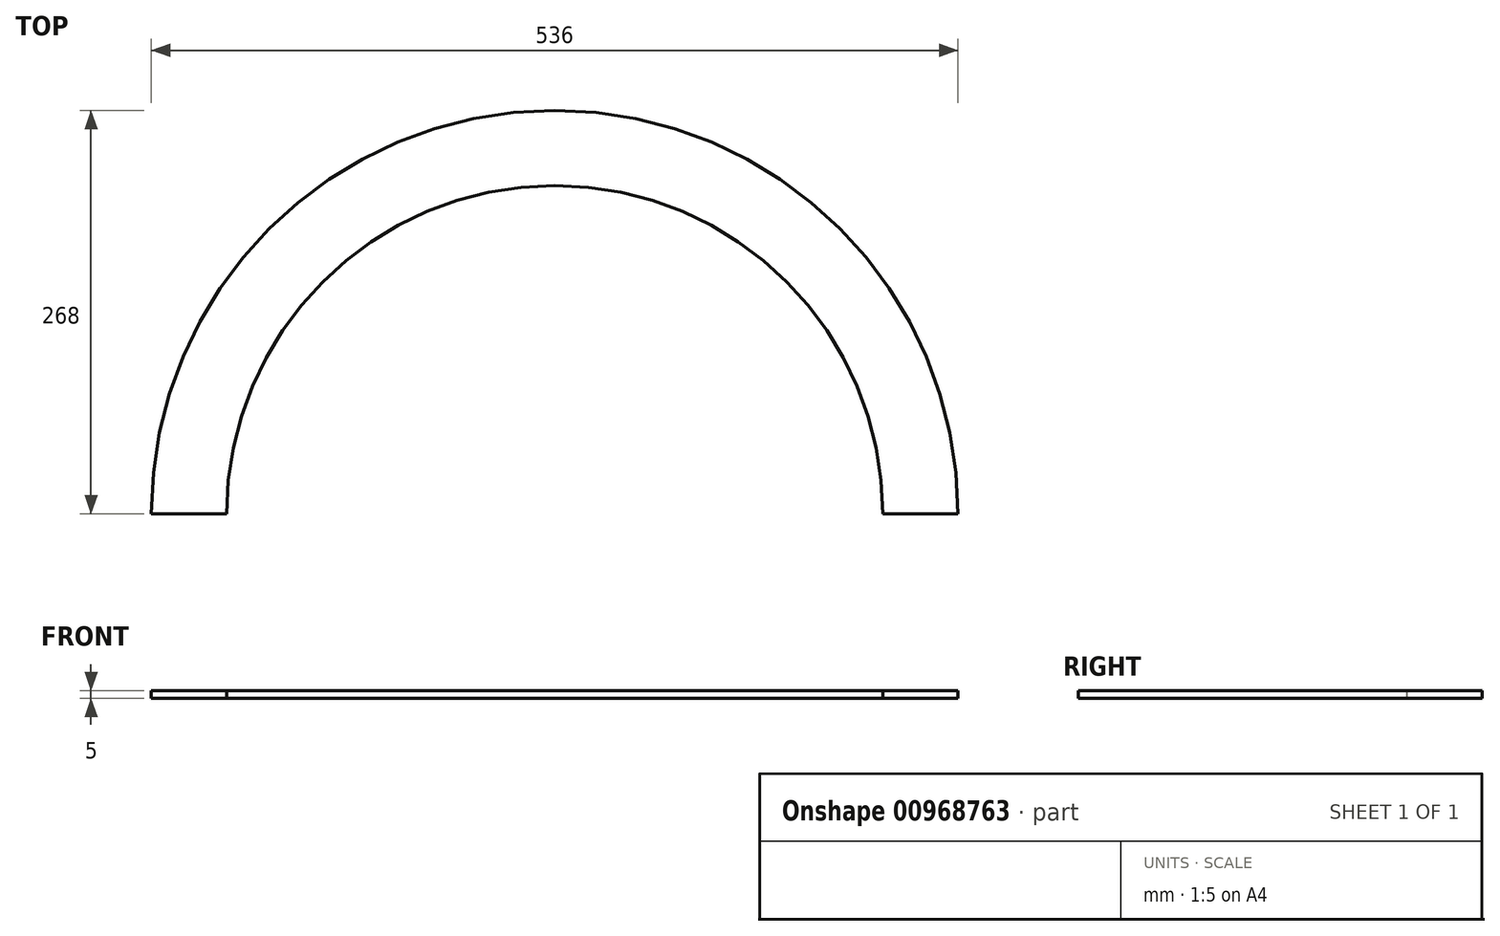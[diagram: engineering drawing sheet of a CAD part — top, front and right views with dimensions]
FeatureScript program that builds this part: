
annotation { "Feature Type Name" : "Feature", "Feature Type Description" : "" }
export const myFeature = defineFeature(function(context is Context, id is Id, definition is map)
    precondition{}
    {
        {
            var Q0;
            Q0=qCreatedBy(makeId("Top.planeOp"),FACE);
            var sketch = newSketch(context, id + "F0", { "sketchPlane" : qUnion([Q0])});
            skArc(sketch, "E0", {"start": v(218, 0) * mm, "mid": v(0, 218) * mm, "end": v(-218, 0) * mm});
            skArc(sketch, "E1", {"start": v(268, 0) * mm, "mid": v(0, 268) * mm, "end": v(-268, 0) * mm});
            skLineSegment(sketch, "E2", {"start": v(218, 0) * mm, "end": v(268, 0) * mm});
            skLineSegment(sketch, "E3", {"start": v(-218, 0) * mm, "end": v(-268, 0) * mm});
            skSolve(sketch);
        }
        {
            var Q0;
            Q0 = qSketchRegion(id + "F0", true);
            extrude(context, id + "F1", {"entities" : qUnion([Q0]), "depth" : 5 * mm, "offsetDistance" : 25 * mm});
        }
    });
